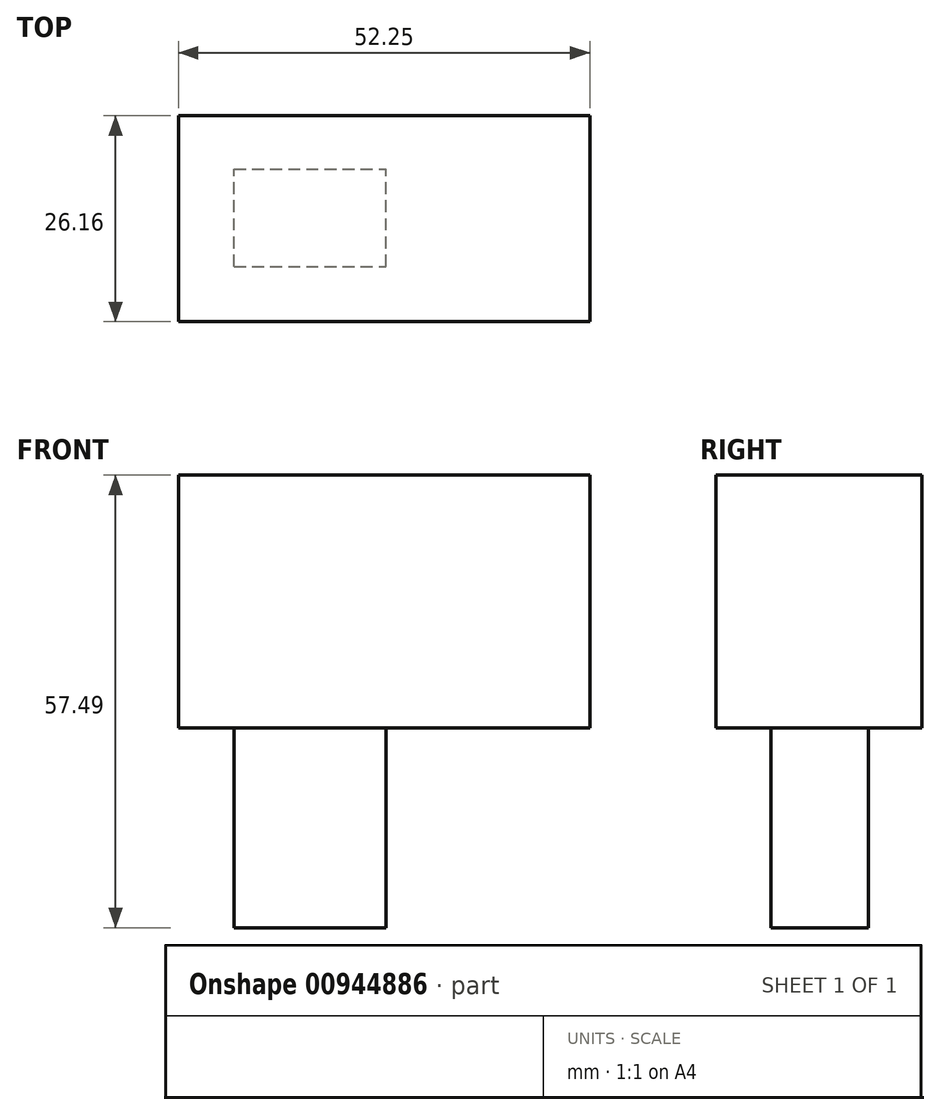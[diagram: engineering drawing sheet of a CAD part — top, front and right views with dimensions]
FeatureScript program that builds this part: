
annotation { "Feature Type Name" : "Feature", "Feature Type Description" : "" }
export const myFeature = defineFeature(function(context is Context, id is Id, definition is map)
    precondition{}
    {
        {
            var Q0;
            Q0=qCreatedBy(makeId("Front.planeOp"),FACE);
            var sketch = newSketch(context, id + "F0", { "sketchPlane" : qUnion([Q0])});
            skLineSegment(sketch, "E0", {"start": v(0, 32.1) * mm, "end": v(52.25, 32.1) * mm});
            skLineSegment(sketch, "E1", {"start": v(52.25, 32.1) * mm, "end": v(52.25, 0) * mm});
            skLineSegment(sketch, "E2", {"start": v(52.25, 0) * mm, "end": v(0, 0) * mm});
            skLineSegment(sketch, "E3", {"start": v(0, 0) * mm, "end": v(0, 32.1) * mm});
            skSolve(sketch);
        }
        {
            var Q0;
            Q0 = qSketchRegion(id + "F0", true);
            var Q1;
            Q1 = qSketchRegion(id + "F2", true);
            extrude(context, id + "F1", {"entities" : qUnion([Q0, Q1]), "depth" : 26.16 * mm, "offsetDistance" : 25.4 * mm});
        }
        {
            var Q0;
            Q0=makeQuery(id+"F1.opExtrude","SWEPT_FACE",FACE,{"disambiguationData":[OSD([sQuery(id+"F0.wireOp",EDGE,"E2")])]});
            var sketch = newSketch(context, id + "F2", { "sketchPlane" : qUnion([Q0])});
            skLineSegment(sketch, "E4.bottom", {"start": v(7.05, 19.14) * mm, "end": v(26.33, 19.14) * mm});
            skLineSegment(sketch, "E4.top", {"start": v(7.05, 6.76) * mm, "end": v(26.33, 6.76) * mm});
            skLineSegment(sketch, "E4.left", {"start": v(7.05, 19.14) * mm, "end": v(7.05, 6.76) * mm});
            skLineSegment(sketch, "E4.right", {"start": v(26.33, 19.14) * mm, "end": v(26.33, 6.76) * mm});
            skSolve(sketch);
        }
        {
            var Q0;
            Q0=makeQuery(id+"F2.imprint","IMPRINT",FACE,{"disambiguationData":[TD([[makeQuery(id+"F2.imprint","IMPRINT",EDGE,{"derivedFrom":sQuery(id+"F2.wireOp",EDGE,"E4.bottom")}),-1.0]])]});
            extrude(context, id + "F3", {"entities" : qUnion([Q0]), "operationType" : NewBodyOperationType.ADD, "depth" : 25.4 * mm, "offsetDistance" : 25.4 * mm});
        }
    });
